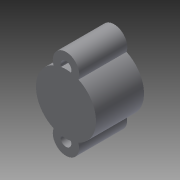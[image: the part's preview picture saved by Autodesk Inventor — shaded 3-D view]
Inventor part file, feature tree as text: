
AUTODESK INVENTOR PART (.ipt)
format: ipt  version: 2015 (Build 190159000, 159)  size: 97,792 bytes
history: native  units: mm
features: extrude x1, sketch x1
ambient origin geometry x8: Origin, YZ Plane, XZ Plane, XY Plane, X Axis, Y Axis, Z Axis, Center Point
bodies: Solid1 (feature_tree)
feature tree (2):
  extrude  "Extrusion1"  Depth=10.16mm
  sketch  "Sketch1"  dims[d0=12.7mm d1=2.286mm d2=2.286mm d3=6.731mm d4=6.731mm d5=13.462mm d6=19.05mm d7=10.16mm d8=0.0mm]
